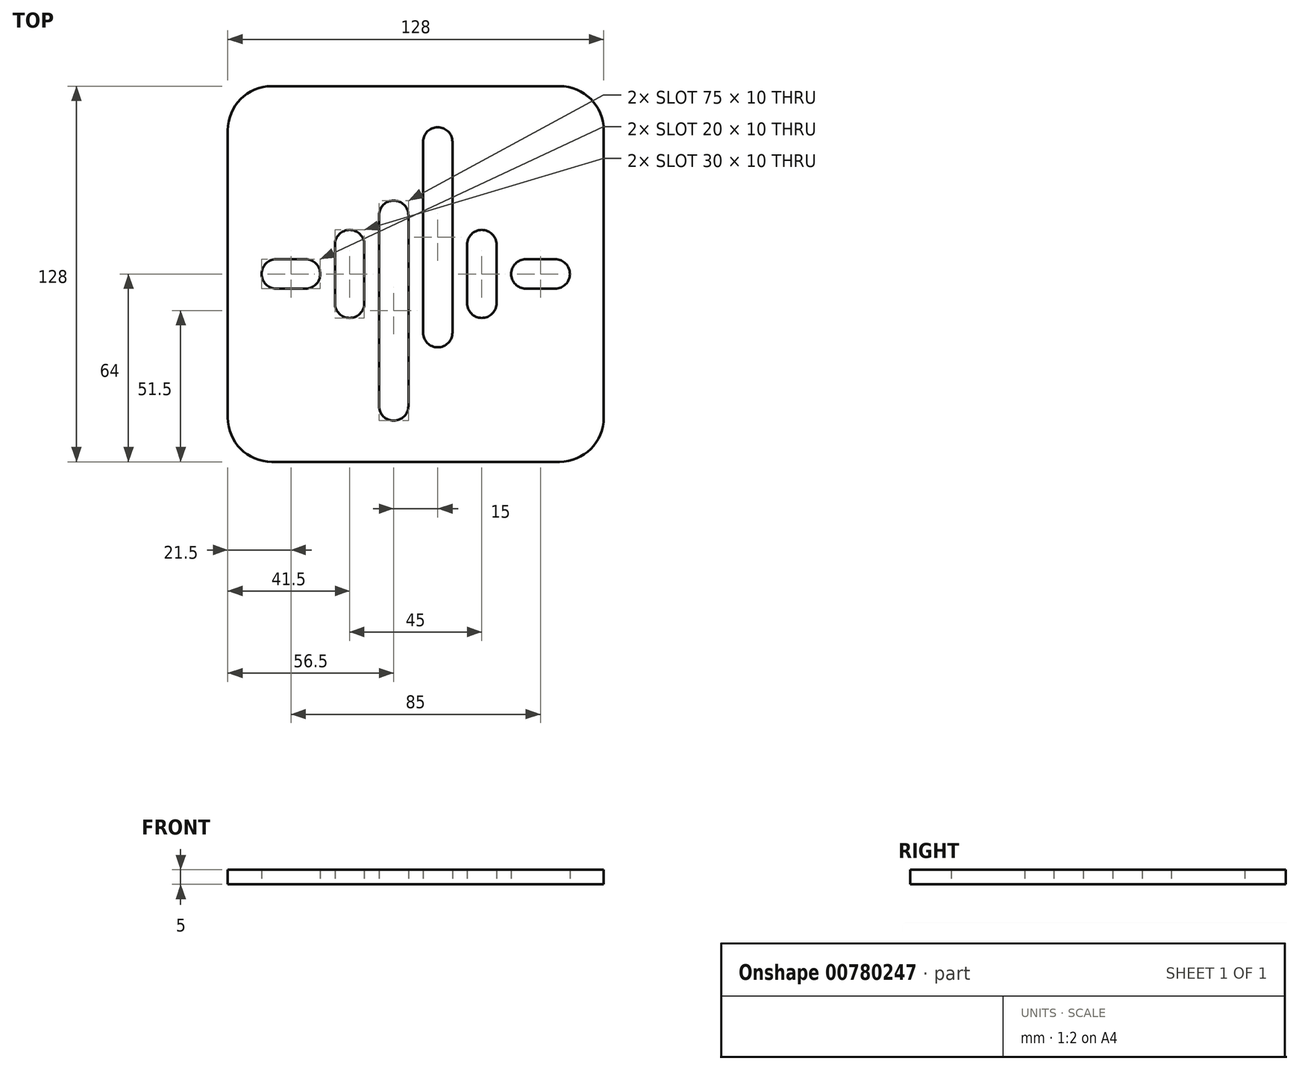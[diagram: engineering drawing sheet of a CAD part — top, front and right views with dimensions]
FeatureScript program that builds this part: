
annotation { "Feature Type Name" : "Feature", "Feature Type Description" : "" }
export const myFeature = defineFeature(function(context is Context, id is Id, definition is map)
    precondition{}
    {
        {
            var Q0;
            Q0=qCreatedBy(makeId("Top.planeOp"),FACE);
            var sketch = newSketch(context, id + "F0", { "sketchPlane" : qUnion([Q0])});
            skLineSegment(sketch, "E0.bottom", {"start": v(49, 64) * mm, "end": v(-49, 64) * mm});
            skLineSegment(sketch, "E0.top", {"start": v(49, -64) * mm, "end": v(-49, -64) * mm});
            skLineSegment(sketch, "E0.left", {"start": v(64, 49) * mm, "end": v(64, -49) * mm});
            skLineSegment(sketch, "E0.right", {"start": v(-64, 49) * mm, "end": v(-64, -49) * mm});
            skPoint(sketch, "E0.middle", {"position": v(0, 0) * mm});
            skPoint(sketch, "E1.visualSharp", {"position": v(-64, 64) * mm});
            skArc(sketch, "E1.filletArc", {"start": v(-49, 64) * mm, "mid": v(-59.6, 59.6) * mm, "end": v(-64, 49) * mm});
            skPoint(sketch, "E2.visualSharp", {"position": v(64, 64) * mm});
            skArc(sketch, "E2.filletArc", {"start": v(64, 49) * mm, "mid": v(59.6, 59.6) * mm, "end": v(49, 64) * mm});
            skPoint(sketch, "E3.visualSharp", {"position": v(64, -64) * mm});
            skArc(sketch, "E3.filletArc", {"start": v(49, -64) * mm, "mid": v(59.6, -59.6) * mm, "end": v(64, -49) * mm});
            skPoint(sketch, "E4.visualSharp", {"position": v(-64, -64) * mm});
            skArc(sketch, "E4.filletArc", {"start": v(-64, -49) * mm, "mid": v(-59.6, -59.6) * mm, "end": v(-49, -64) * mm});
            skLineSegment(sketch, "E5.bottom", {"start": v(-37.5, 5) * mm, "end": v(-47.5, 5) * mm});
            skLineSegment(sketch, "E5.top", {"start": v(-37.5, -5) * mm, "end": v(-47.5, -5) * mm});
            skLineSegment(sketch, "E5.left", {"start": v(-32.5, 0) * mm, "end": v(-32.5, 0) * mm});
            skLineSegment(sketch, "E5.right", {"start": v(-52.5, 0) * mm, "end": v(-52.5, 0) * mm});
            skPoint(sketch, "E5.middle", {"position": v(-42.5, 0) * mm});
            skPoint(sketch, "E6.visualSharp", {"position": v(-32.5, 5) * mm});
            skArc(sketch, "E6.filletArc", {"start": v(-32.5, 0) * mm, "mid": v(-33.96, 3.54) * mm, "end": v(-37.5, 5) * mm});
            skPoint(sketch, "E7.visualSharp", {"position": v(-52.5, 5) * mm});
            skArc(sketch, "E7.filletArc", {"start": v(-47.5, 5) * mm, "mid": v(-51.04, 3.54) * mm, "end": v(-52.5, 0) * mm});
            skPoint(sketch, "E8.visualSharp", {"position": v(-52.5, -5) * mm});
            skArc(sketch, "E8.filletArc", {"start": v(-52.5, 0) * mm, "mid": v(-51.04, -3.54) * mm, "end": v(-47.5, -5) * mm});
            skPoint(sketch, "E9.visualSharp", {"position": v(-32.5, -5) * mm});
            skArc(sketch, "E9.filletArc", {"start": v(-37.5, -5) * mm, "mid": v(-33.96, -3.54) * mm, "end": v(-32.5, 0) * mm});
            skLineSegment(sketch, "E10.bottom", {"start": v(-22.5, 15) * mm, "end": v(-22.5, 15) * mm});
            skLineSegment(sketch, "E10.top", {"start": v(-22.5, -15) * mm, "end": v(-22.5, -15) * mm});
            skLineSegment(sketch, "E10.left", {"start": v(-17.5, 10) * mm, "end": v(-17.5, -10) * mm});
            skLineSegment(sketch, "E10.right", {"start": v(-27.5, 10) * mm, "end": v(-27.5, -10) * mm});
            skPoint(sketch, "E10.middle", {"position": v(-22.5, 0) * mm});
            skLineSegment(sketch, "E11.bottom", {"start": v(-7.5, 25) * mm, "end": v(-7.5, 25) * mm});
            skLineSegment(sketch, "E11.top", {"start": v(-2.5, -25) * mm, "end": v(-12.5, -25) * mm, "construction": true});
            skLineSegment(sketch, "E11.left", {"start": v(-2.5, 20) * mm, "end": v(-2.5, -25) * mm});
            skLineSegment(sketch, "E11.right", {"start": v(-12.5, 20) * mm, "end": v(-12.5, -25) * mm});
            skPoint(sketch, "E11.middle", {"position": v(-7.5, 0) * mm});
            skLineSegment(sketch, "E12", {"start": v(-12.5, -25) * mm, "end": v(-12.5, -45) * mm});
            skLineSegment(sketch, "E13", {"start": v(-2.5, -25) * mm, "end": v(-2.5, -45) * mm});
            skLineSegment(sketch, "E14", {"start": v(-7.5, -50) * mm, "end": v(-7.5, -50) * mm});
            skPoint(sketch, "E15.visualSharp", {"position": v(-12.5, -50) * mm});
            skArc(sketch, "E15.filletArc", {"start": v(-12.5, -45) * mm, "mid": v(-11.04, -48.54) * mm, "end": v(-7.5, -50) * mm});
            skPoint(sketch, "E16.visualSharp", {"position": v(-2.5, -50) * mm});
            skArc(sketch, "E16.filletArc", {"start": v(-7.5, -50) * mm, "mid": v(-3.96, -48.54) * mm, "end": v(-2.5, -45) * mm});
            skPoint(sketch, "E17.visualSharp", {"position": v(-27.5, -15) * mm});
            skArc(sketch, "E17.filletArc", {"start": v(-27.5, -10) * mm, "mid": v(-26.04, -13.54) * mm, "end": v(-22.5, -15) * mm});
            skPoint(sketch, "E18.visualSharp", {"position": v(-17.5, -15) * mm});
            skArc(sketch, "E18.filletArc", {"start": v(-22.5, -15) * mm, "mid": v(-18.96, -13.54) * mm, "end": v(-17.5, -10) * mm});
            skPoint(sketch, "E19.visualSharp", {"position": v(-27.5, 15) * mm});
            skArc(sketch, "E19.filletArc", {"start": v(-22.5, 15) * mm, "mid": v(-26.04, 13.54) * mm, "end": v(-27.5, 10) * mm});
            skPoint(sketch, "E20.visualSharp", {"position": v(-17.5, 15) * mm});
            skArc(sketch, "E20.filletArc", {"start": v(-17.5, 10) * mm, "mid": v(-18.96, 13.54) * mm, "end": v(-22.5, 15) * mm});
            skPoint(sketch, "E21.visualSharp", {"position": v(-12.5, 25) * mm});
            skArc(sketch, "E21.filletArc", {"start": v(-7.5, 25) * mm, "mid": v(-11.04, 23.54) * mm, "end": v(-12.5, 20) * mm});
            skPoint(sketch, "E22.visualSharp", {"position": v(-2.5, 25) * mm});
            skArc(sketch, "E22.filletArc", {"start": v(-2.5, 20) * mm, "mid": v(-3.96, 23.54) * mm, "end": v(-7.5, 25) * mm});
            skLineSegment(sketch, "E23.1.0", {"start": v(2.5, -20) * mm, "end": v(2.5, 25) * mm});
            skArc(sketch, "E23.1.1", {"start": v(2.5, -20) * mm, "mid": v(3.96, -23.54) * mm, "end": v(7.5, -25) * mm});
            skArc(sketch, "E23.1.2", {"start": v(7.5, -25) * mm, "mid": v(11.04, -23.54) * mm, "end": v(12.5, -20) * mm});
            skLineSegment(sketch, "E23.1.3", {"start": v(12.5, -20) * mm, "end": v(12.5, 25) * mm});
            skLineSegment(sketch, "E23.1.4", {"start": v(12.5, 25) * mm, "end": v(12.5, 45) * mm});
            skLineSegment(sketch, "E23.1.5", {"start": v(2.5, 25) * mm, "end": v(2.5, 45) * mm});
            skArc(sketch, "E23.1.6", {"start": v(12.5, 45) * mm, "mid": v(11.04, 48.54) * mm, "end": v(7.5, 50) * mm});
            skArc(sketch, "E23.1.7", {"start": v(7.5, 50) * mm, "mid": v(3.96, 48.54) * mm, "end": v(2.5, 45) * mm});
            skLineSegment(sketch, "E23.1.8", {"start": v(27.5, -10) * mm, "end": v(27.5, 10) * mm});
            skArc(sketch, "E23.1.9", {"start": v(27.5, 10) * mm, "mid": v(26.04, 13.54) * mm, "end": v(22.5, 15) * mm});
            skArc(sketch, "E23.1.10", {"start": v(22.5, 15) * mm, "mid": v(18.96, 13.54) * mm, "end": v(17.5, 10) * mm});
            skLineSegment(sketch, "E23.1.11", {"start": v(17.5, -10) * mm, "end": v(17.5, 10) * mm});
            skArc(sketch, "E23.1.12", {"start": v(17.5, -10) * mm, "mid": v(18.96, -13.54) * mm, "end": v(22.5, -15) * mm});
            skArc(sketch, "E23.1.13", {"start": v(22.5, -15) * mm, "mid": v(26.04, -13.54) * mm, "end": v(27.5, -10) * mm});
            skLineSegment(sketch, "E23.1.14", {"start": v(37.5, -5) * mm, "end": v(47.5, -5) * mm});
            skArc(sketch, "E23.1.15", {"start": v(47.5, -5) * mm, "mid": v(51.04, -3.54) * mm, "end": v(52.5, 0) * mm});
            skArc(sketch, "E23.1.16", {"start": v(52.5, 0) * mm, "mid": v(51.04, 3.54) * mm, "end": v(47.5, 5) * mm});
            skLineSegment(sketch, "E23.1.17", {"start": v(37.5, 5) * mm, "end": v(47.5, 5) * mm});
            skArc(sketch, "E23.1.18", {"start": v(37.5, 5) * mm, "mid": v(33.96, 3.54) * mm, "end": v(32.5, 0) * mm});
            skArc(sketch, "E23.1.19", {"start": v(32.5, 0) * mm, "mid": v(33.96, -3.54) * mm, "end": v(37.5, -5) * mm});
            skLineSegment(sketch, "E23.anchor1", {"start": v(0, 0) * mm, "end": v(-2.5, -25) * mm, "construction": true});
            skLineSegment(sketch, "E23.anchor2", {"start": v(0, 0) * mm, "end": v(2.5, 25) * mm, "construction": true});
            skSolve(sketch);
        }
        {
            var Q0;
            Q0=makeQuery(id+"F0.imprint","IMPRINT",FACE,{"disambiguationData":[TD([[makeQuery(id+"F0.imprint","IMPRINT",EDGE,{"derivedFrom":sQuery(id+"F0.wireOp",EDGE,"E0.bottom")}),1.0]])]});
            extrude(context, id + "F1", {"entities" : qUnion([Q0]), "depth" : 5 * mm, "offsetDistance" : 25 * mm});
        }
        {
            var Q0;
            Q0=makeQuery(id+"F0.imprint","IMPRINT",FACE,{"disambiguationData":[TD([[makeQuery(id+"F0.imprint","IMPRINT",EDGE,{"derivedFrom":sQuery(id+"F0.wireOp",EDGE,"E5.bottom")}),1.0]])]});
            extrude(context, id + "F2", {"entities" : qUnion([Q0]), "depth" : 5 * mm, "offsetDistance" : 25 * mm});
        }
        {
            var Q0;
            Q0=makeQuery(id+"F0.imprint","IMPRINT",FACE,{"disambiguationData":[TD([[makeQuery(id+"F0.imprint","IMPRINT",EDGE,{"derivedFrom":sQuery(id+"F0.wireOp",EDGE,"E10.left")}),-1.0]])]});
            extrude(context, id + "F3", {"entities" : qUnion([Q0]), "depth" : 5 * mm, "offsetDistance" : 25 * mm});
        }
        {
            var Q0;
            Q0=makeQuery(id+"F0.imprint","IMPRINT",FACE,{"disambiguationData":[TD([[makeQuery(id+"F0.imprint","IMPRINT",EDGE,{"derivedFrom":sQuery(id+"F0.wireOp",EDGE,"E11.left")}),-1.0]])]});
            extrude(context, id + "F4", {"entities" : qUnion([Q0]), "depth" : 5 * mm, "offsetDistance" : 25 * mm});
        }
        {
            var Q0;
            Q0=makeQuery(id+"F0.imprint","IMPRINT",FACE,{"disambiguationData":[TD([[makeQuery(id+"F0.imprint","IMPRINT",EDGE,{"derivedFrom":sQuery(id+"F0.wireOp",EDGE,"E23.1.0")}),-1.0]])]});
            extrude(context, id + "F5", {"entities" : qUnion([Q0]), "depth" : 5 * mm, "offsetDistance" : 25 * mm});
        }
        {
            var Q0;
            Q0=makeQuery(id+"F0.imprint","IMPRINT",FACE,{"disambiguationData":[TD([[makeQuery(id+"F0.imprint","IMPRINT",EDGE,{"derivedFrom":sQuery(id+"F0.wireOp",EDGE,"E23.1.8")}),1.0]])]});
            extrude(context, id + "F6", {"entities" : qUnion([Q0]), "depth" : 5 * mm, "offsetDistance" : 25 * mm});
        }
        {
            var Q0;
            Q0=makeQuery(id+"F0.imprint","IMPRINT",FACE,{"disambiguationData":[TD([[makeQuery(id+"F0.imprint","IMPRINT",EDGE,{"derivedFrom":sQuery(id+"F0.wireOp",EDGE,"E23.1.14")}),1.0]])]});
            extrude(context, id + "F7", {"entities" : qUnion([Q0]), "depth" : 5 * mm, "offsetDistance" : 25 * mm});
        }
    });
